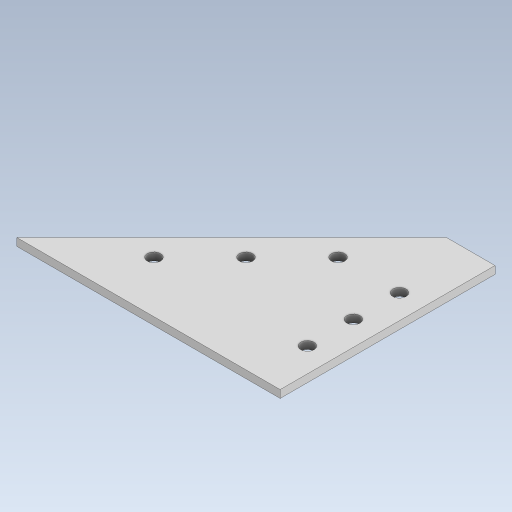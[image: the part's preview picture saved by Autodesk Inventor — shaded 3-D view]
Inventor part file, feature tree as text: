
AUTODESK INVENTOR PART (.ipt)
format: ipt  version: 2023 (Build 270158000, 158)  size: 114,176 bytes
history: native  units: in
note: dims shown in document units (in); Inventor stores cm internally (conversion verified against a paired STEP export)
features: sketch x1, extrude x1, hole x1
ambient origin geometry x8: Origin, YZ Plane, XZ Plane, XY Plane, X Axis, Y Axis, Z Axis, Center Point
bodies: Solid1 (feature_tree)
feature tree (3):
  sketch  "Sketch1"  dims[d0=4.0in d1=4.0in d2=0.7874in d3=0.7874in d4=45.0deg d11=0.3937in d13=0.3937in d15=1.0in d16=1.5in d17=3.5in d19=0.125in d20=0.0in d21=0.217in d22=0.472in d23=0.409in d24=0.25in d25=90.0deg d26=1.0in d27=0.8108in d28=0.0in d29=0.0in d30=0.0in d31=0.0in]
  extrude  "Extrusion1"  Depth=0.125in
  hole  "Hole1"  [1 undecoded]
note: 1 required parameter value undecoded (feature->parameter linkage not recoverable at this tier; creation-order binding heuristic only, values carry confidence <= 0.55)
